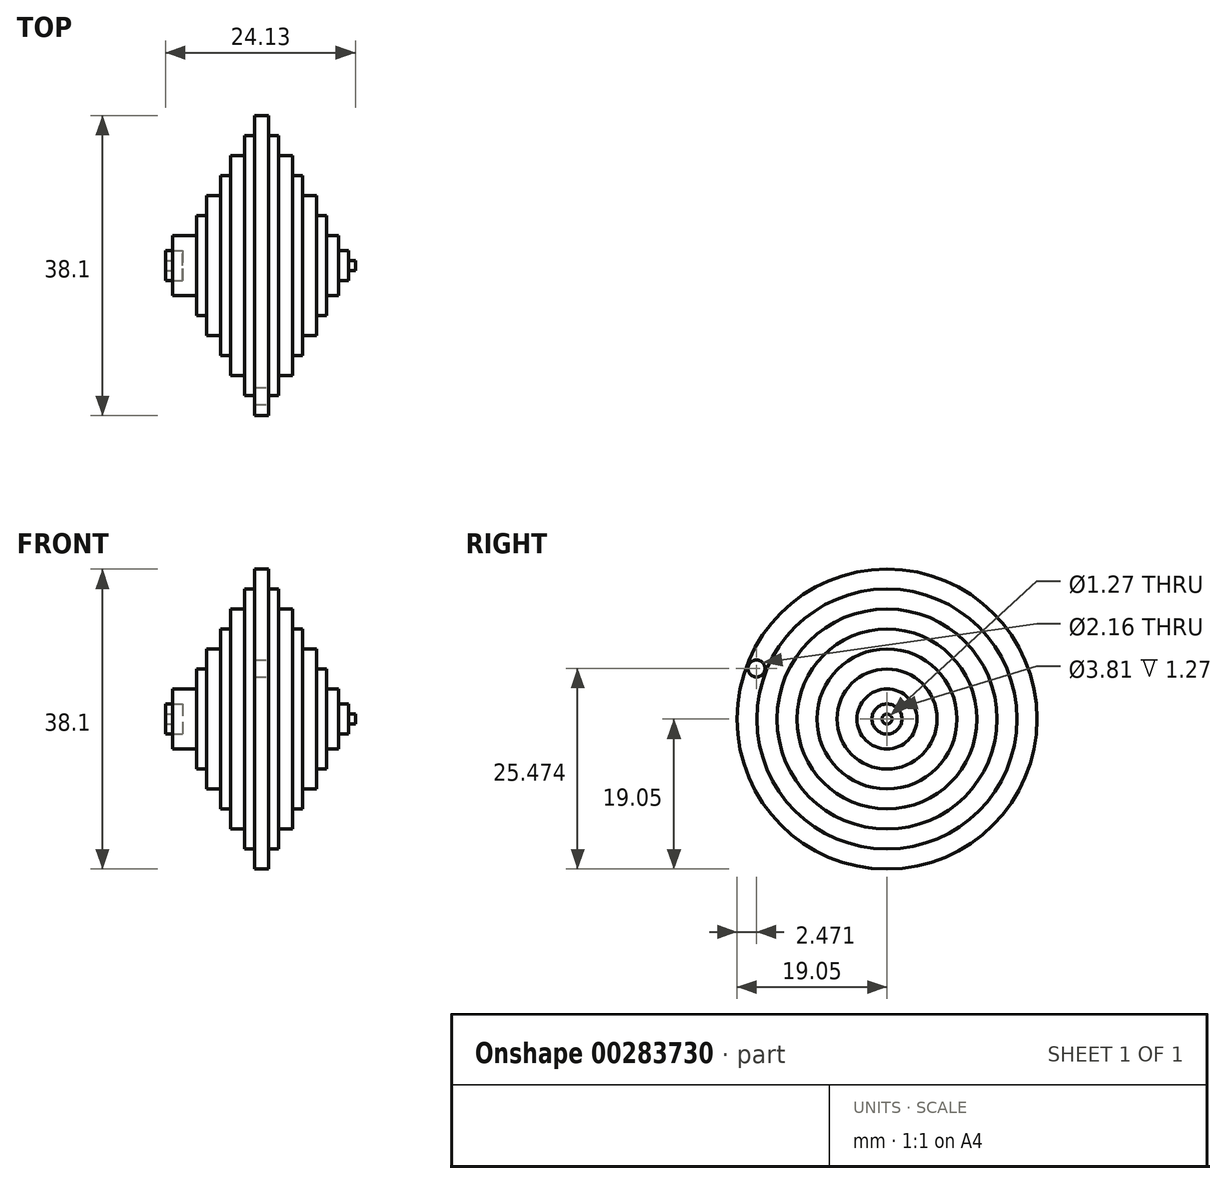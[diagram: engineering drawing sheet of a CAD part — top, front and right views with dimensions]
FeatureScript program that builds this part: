
annotation { "Feature Type Name" : "Feature", "Feature Type Description" : "" }
export const myFeature = defineFeature(function(context is Context, id is Id, definition is map)
    precondition{}
    {
        {
            var Q0;
            Q0=qCreatedBy(makeId("Right.planeOp"),FACE);
            var sketch = newSketch(context, id + "F0", { "sketchPlane" : qUnion([Q0])});
            skLineSegment(sketch, "E0", {"start": v(0, 0) * mm, "end": v(0, 38.1) * mm});
            skLineSegment(sketch, "E1", {"start": v(0, 38.1) * mm, "end": v(-38.1, 38.1) * mm});
            skLineSegment(sketch, "E2", {"start": v(-38.1, 38.1) * mm, "end": v(-38.1, 0) * mm});
            skLineSegment(sketch, "E3", {"start": v(-38.1, 0) * mm, "end": v(0, 0) * mm});
            skPoint(sketch, "E4.start.orphan", {"position": v(0.74, 0) * mm});
            skCircle(sketch, "E5", {"center": v(-19.05, 19.05) * mm, "radius": 19.05 * mm});
            skPoint(sketch, "E6.orphan", {"position": v(-19.05, 38.1) * mm});
            skPoint(sketch, "E7.end.orphan", {"position": v(-19.05, 0) * mm});
            skSolve(sketch);
        }
        {
            var Q0;
            {var subQ0=sQuery(id+"F0.wireOp",EDGE,"E5");var subQ1=makeQuery(id+"F0.imprint","INTERSECT",VERTEX,{"derivedFrom":[sQuery(id+"F0.wireOp",EDGE,"E0"),subQ0]});Q0=makeQuery(id+"F0.imprint","IMPRINT",FACE,{"disambiguationData":[TD([[makeQuery(id+"F0.imprint","IMPRINT",EDGE,{"disambiguationData":[TD([[subQ1,-1.0]])],"derivedFrom":subQ0}),1.0]])]});}
            extrude(context, id + "F1", {"entities" : qUnion([Q0]), "depth" : 1.78 * mm});
        }
        {
            var Q0;
            Q0=makeQuery(id+"F1.opExtrude","CAP_FACE",FACE,{"disambiguationData":[OSD([sQuery(id+"F0.wireOp",EDGE,"E5")])],"isStart":false});
            var sketch = newSketch(context, id + "F2", { "sketchPlane" : qUnion([Q0])});
            skLineSegment(sketch, "E8", {"start": v(0, 0) * mm, "end": v(0, 38.1) * mm});
            skLineSegment(sketch, "E9", {"start": v(0, 38.1) * mm, "end": v(-38.1, 38.1) * mm});
            skLineSegment(sketch, "E10", {"start": v(-38.1, 38.1) * mm, "end": v(-38.1, 0) * mm});
            skLineSegment(sketch, "E11", {"start": v(-38.1, 0) * mm, "end": v(0, 0) * mm});
            skCircle(sketch, "E12", {"center": v(-19.05, 19.05) * mm, "radius": 16.51 * mm});
            skPoint(sketch, "E13.start.orphan", {"position": v(-19.05, 38.1) * mm});
            skPoint(sketch, "E14.trimOffspring.end.orphan", {"position": v(-19.05, 0) * mm});
            skSolve(sketch);
        }
        {
            var Q0;
            Q0=makeQuery(id+"F2.imprint","IMPRINT",FACE,{"disambiguationData":[TD([[makeQuery(id+"F2.imprint","IMPRINT",EDGE,{"derivedFrom":sQuery(id+"F2.wireOp",EDGE,"E12")}),1.0]])]});
            extrude(context, id + "F3", {"entities" : qUnion([Q0]), "operationType" : NewBodyOperationType.ADD, "depth" : 1.27 * mm});
        }
        {
            var Q0;
            Q0=makeQuery(id+"F3.opExtrude","CAP_FACE",FACE,{"disambiguationData":[OSD([sQuery(id+"F2.wireOp",EDGE,"E12")])],"isStart":false});
            var sketch = newSketch(context, id + "F4", { "sketchPlane" : qUnion([Q0])});
            skLineSegment(sketch, "E15", {"start": v(0, 0) * mm, "end": v(-38.1, 0) * mm});
            skLineSegment(sketch, "E16", {"start": v(0, 38.1) * mm, "end": v(0, 0) * mm});
            skLineSegment(sketch, "E17", {"start": v(0, 38.1) * mm, "end": v(-38.1, 38.1) * mm});
            skLineSegment(sketch, "E18", {"start": v(-38.1, 38.1) * mm, "end": v(-38.1, 0) * mm});
            skCircle(sketch, "E19", {"center": v(-19.05, 19.05) * mm, "radius": 13.97 * mm});
            skPoint(sketch, "E20.start.orphan", {"position": v(-19.05, 38.1) * mm});
            skPoint(sketch, "E21.trimOffspring.end.orphan", {"position": v(-19.05, 0) * mm});
            skSolve(sketch);
        }
        {
            var Q0;
            Q0=makeQuery(id+"F4.imprint","IMPRINT",FACE,{"disambiguationData":[TD([[makeQuery(id+"F4.imprint","IMPRINT",EDGE,{"derivedFrom":sQuery(id+"F4.wireOp",EDGE,"E19")}),1.0]])]});
            extrude(context, id + "F5", {"entities" : qUnion([Q0]), "operationType" : NewBodyOperationType.ADD, "depth" : 1.78 * mm});
        }
        {
            var Q0;
            Q0=makeQuery(id+"F5.opExtrude","CAP_FACE",FACE,{"disambiguationData":[OSD([sQuery(id+"F4.wireOp",EDGE,"E19")])],"isStart":false});
            var sketch = newSketch(context, id + "F6", { "sketchPlane" : qUnion([Q0])});
            skLineSegment(sketch, "E22", {"start": v(0, 0) * mm, "end": v(0, 38.1) * mm});
            skLineSegment(sketch, "E23", {"start": v(0, 38.1) * mm, "end": v(-38.1, 38.1) * mm});
            skLineSegment(sketch, "E24", {"start": v(-38.1, 38.1) * mm, "end": v(-38.1, 0) * mm});
            skLineSegment(sketch, "E25", {"start": v(-38.1, 0) * mm, "end": v(0, 0) * mm});
            skCircle(sketch, "E26", {"center": v(-19.05, 19.05) * mm, "radius": 11.43 * mm});
            skPoint(sketch, "E27.start.orphan", {"position": v(-19.05, 38.1) * mm});
            skPoint(sketch, "E28.trimOffspring.end.orphan", {"position": v(-19.05, 0) * mm});
            skSolve(sketch);
        }
        {
            var Q0;
            Q0=makeQuery(id+"F6.imprint","IMPRINT",FACE,{"disambiguationData":[TD([[makeQuery(id+"F6.imprint","IMPRINT",EDGE,{"derivedFrom":sQuery(id+"F6.wireOp",EDGE,"E26")}),1.0]])]});
            extrude(context, id + "F7", {"entities" : qUnion([Q0]), "operationType" : NewBodyOperationType.ADD, "depth" : 1.27 * mm});
        }
        {
            var Q0;
            Q0=makeQuery(id+"F7.opExtrude","CAP_FACE",FACE,{"disambiguationData":[OSD([sQuery(id+"F6.wireOp",EDGE,"E26")])],"isStart":false});
            var sketch = newSketch(context, id + "F8", { "sketchPlane" : qUnion([Q0])});
            skLineSegment(sketch, "E29", {"start": v(0, 0) * mm, "end": v(0, 38.1) * mm});
            skLineSegment(sketch, "E30", {"start": v(0, 38.1) * mm, "end": v(-38.1, 38.1) * mm});
            skLineSegment(sketch, "E31", {"start": v(-38.1, 38.1) * mm, "end": v(-38.1, 0) * mm});
            skLineSegment(sketch, "E32", {"start": v(-38.1, 0) * mm, "end": v(0, 0) * mm});
            skCircle(sketch, "E33", {"center": v(-19.05, 19.05) * mm, "radius": 8.9 * mm});
            skPoint(sketch, "E34.start.orphan", {"position": v(-19.05, 38.1) * mm});
            skPoint(sketch, "E35.trimOffspring.end.orphan", {"position": v(-19.05, 0) * mm});
            skSolve(sketch);
        }
        {
            var Q0;
            Q0=makeQuery(id+"F8.imprint","IMPRINT",FACE,{"disambiguationData":[TD([[makeQuery(id+"F8.imprint","IMPRINT",EDGE,{"derivedFrom":sQuery(id+"F8.wireOp",EDGE,"E33")}),1.0]])]});
            extrude(context, id + "F9", {"entities" : qUnion([Q0]), "operationType" : NewBodyOperationType.ADD, "depth" : 1.78 * mm});
        }
        {
            var Q0;
            Q0=makeQuery(id+"F9.opExtrude","CAP_FACE",FACE,{"disambiguationData":[OSD([sQuery(id+"F8.wireOp",EDGE,"E33")])],"isStart":false});
            var sketch = newSketch(context, id + "F10", { "sketchPlane" : qUnion([Q0])});
            skLineSegment(sketch, "E36", {"start": v(0, 0) * mm, "end": v(0, 38.1) * mm});
            skLineSegment(sketch, "E37", {"start": v(0, 38.1) * mm, "end": v(-38.1, 38.1) * mm});
            skLineSegment(sketch, "E38", {"start": v(-38.1, 38.1) * mm, "end": v(-38.1, 0) * mm});
            skLineSegment(sketch, "E39", {"start": v(-38.1, 0) * mm, "end": v(0, -0.59) * mm});
            skCircle(sketch, "E40", {"center": v(-19.05, 19.05) * mm, "radius": 6.35 * mm});
            skPoint(sketch, "E41.orphan", {"position": v(-19.05, 38.1) * mm});
            skPoint(sketch, "E42.end.orphan", {"position": v(-19.05, -0.3) * mm});
            skSolve(sketch);
        }
        {
            var Q0;
            Q0=makeQuery(id+"F10.imprint","IMPRINT",FACE,{"disambiguationData":[TD([[makeQuery(id+"F10.imprint","IMPRINT",EDGE,{"derivedFrom":sQuery(id+"F10.wireOp",EDGE,"E40")}),1.0]])]});
            extrude(context, id + "F11", {"entities" : qUnion([Q0]), "operationType" : NewBodyOperationType.ADD, "depth" : 1.27 * mm});
        }
        {
            var Q0;
            Q0=makeQuery(id+"F11.opExtrude","CAP_FACE",FACE,{"disambiguationData":[OSD([sQuery(id+"F10.wireOp",EDGE,"E40")])],"isStart":false});
            var sketch = newSketch(context, id + "F12", { "sketchPlane" : qUnion([Q0])});
            skLineSegment(sketch, "E43", {"start": v(0, 0) * mm, "end": v(0, 38.1) * mm});
            skLineSegment(sketch, "E44", {"start": v(0, 38.1) * mm, "end": v(-38.1, 38.1) * mm});
            skLineSegment(sketch, "E45", {"start": v(-38.1, 38.1) * mm, "end": v(-38.1, 0) * mm});
            skLineSegment(sketch, "E46", {"start": v(-38.1, 0) * mm, "end": v(0, 0) * mm});
            skCircle(sketch, "E47", {"center": v(-19.05, 19.05) * mm, "radius": 3.81 * mm});
            skPoint(sketch, "E48.orphan", {"position": v(-19.05, 38.1) * mm});
            skPoint(sketch, "E49.end.orphan", {"position": v(-19.05, 0) * mm});
            skSolve(sketch);
        }
        {
            var Q0;
            Q0=makeQuery(id+"F12.imprint","IMPRINT",FACE,{"disambiguationData":[TD([[makeQuery(id+"F12.imprint","IMPRINT",EDGE,{"derivedFrom":sQuery(id+"F12.wireOp",EDGE,"E47")}),1.0]])]});
            extrude(context, id + "F13", {"entities" : qUnion([Q0]), "operationType" : NewBodyOperationType.ADD, "depth" : 1.52 * mm});
        }
        {
            var Q0;
            Q0=makeQuery(id+"F13.opExtrude","CAP_FACE",FACE,{"disambiguationData":[OSD([sQuery(id+"F12.wireOp",EDGE,"E47")])],"isStart":false});
            var sketch = newSketch(context, id + "F14", { "sketchPlane" : qUnion([Q0])});
            skLineSegment(sketch, "E50", {"start": v(0, 0) * mm, "end": v(0, 38.1) * mm});
            skLineSegment(sketch, "E51", {"start": v(0, 38.1) * mm, "end": v(-38.1, 38.1) * mm});
            skLineSegment(sketch, "E52", {"start": v(-38.1, 38.1) * mm, "end": v(-38.1, 0) * mm});
            skLineSegment(sketch, "E53", {"start": v(-38.1, 0) * mm, "end": v(0, 0) * mm});
            skCircle(sketch, "E54", {"center": v(-19.05, 19.05) * mm, "radius": 1.9 * mm});
            skPoint(sketch, "E55.orphan", {"position": v(-19.05, 38.1) * mm});
            skPoint(sketch, "E56.end.orphan", {"position": v(-19.05, 0) * mm});
            skSolve(sketch);
        }
        {
            var Q0;
            Q0=makeQuery(id+"F14.imprint","IMPRINT",FACE,{"disambiguationData":[TD([[makeQuery(id+"F14.imprint","IMPRINT",EDGE,{"derivedFrom":sQuery(id+"F14.wireOp",EDGE,"E54")}),1.0]])]});
            extrude(context, id + "F15", {"entities" : qUnion([Q0]), "operationType" : NewBodyOperationType.ADD, "depth" : 1.27 * mm});
        }
        {
            var Q0;
            Q0=makeQuery(id+"F15.opExtrude","CAP_FACE",FACE,{"disambiguationData":[OSD([sQuery(id+"F14.wireOp",EDGE,"E54")])],"isStart":false});
            var sketch = newSketch(context, id + "F16", { "sketchPlane" : qUnion([Q0])});
            skLineSegment(sketch, "E57", {"start": v(0, 0) * mm, "end": v(0, 38.1) * mm});
            skLineSegment(sketch, "E58", {"start": v(0, 38.1) * mm, "end": v(-38.1, 38.1) * mm});
            skLineSegment(sketch, "E59", {"start": v(-38.1, 38.1) * mm, "end": v(-38.1, 0) * mm});
            skLineSegment(sketch, "E60", {"start": v(-38.1, 0) * mm, "end": v(0, 0) * mm});
            skCircle(sketch, "E61", {"center": v(-19.05, 19.05) * mm, "radius": 0.64 * mm});
            skPoint(sketch, "E62.orphan", {"position": v(-19.05, 38.1) * mm});
            skPoint(sketch, "E63.end.orphan", {"position": v(-19.05, 0) * mm});
            skSolve(sketch);
        }
        {
            var Q0;
            Q0=makeQuery(id+"F16.imprint","IMPRINT",FACE,{"disambiguationData":[TD([[makeQuery(id+"F16.imprint","IMPRINT",EDGE,{"derivedFrom":sQuery(id+"F16.wireOp",EDGE,"E61")}),1.0]])]});
            extrude(context, id + "F17", {"entities" : qUnion([Q0]), "operationType" : NewBodyOperationType.ADD, "depth" : 0.89 * mm});
        }
        {
            var Q0;
            Q0=makeQuery(id+"F1.opExtrude","CAP_FACE",FACE,{"disambiguationData":[OSD([sQuery(id+"F0.wireOp",EDGE,"E5")])],"isStart":false});
            var sketch = newSketch(context, id + "F18", { "sketchPlane" : qUnion([Q0])});
            skCircle(sketch, "E64", {"center": v(-35.63, 25.47) * mm, "radius": 1.08 * mm});
            skPoint(sketch, "E65.trimOffspring.end.orphan", {"position": v(-34.49, 24.9) * mm});
            skPoint(sketch, "E66.start.orphan", {"position": v(-36.77, 26.05) * mm});
            skSolve(sketch);
        }
        {
            var Q0;
            Q0=makeQuery(id+"F18.imprint","IMPRINT",FACE,{"disambiguationData":[TD([[makeQuery(id+"F18.imprint","IMPRINT",EDGE,{"derivedFrom":sQuery(id+"F18.wireOp",EDGE,"E64")}),1.0]])]});
            extrude(context, id + "F19", {"entities" : qUnion([Q0]), "operationType" : NewBodyOperationType.REMOVE, "oppositeDirection" : true, "depth" : 1.78 * mm});
        }
        {
            var Q0;
            Q0=makeQuery(id+"F1.opExtrude","CAP_FACE",FACE,{"disambiguationData":[OSD([sQuery(id+"F0.wireOp",EDGE,"E5")])],"isStart":true});
            var sketch = newSketch(context, id + "F20", { "sketchPlane" : qUnion([Q0])});
            skLineSegment(sketch, "E67", {"start": v(0, 0) * mm, "end": v(0, 38.1) * mm});
            skLineSegment(sketch, "E68", {"start": v(0, 38.1) * mm, "end": v(38.1, 38.1) * mm});
            skLineSegment(sketch, "E69", {"start": v(38.1, 38.1) * mm, "end": v(38.1, 0) * mm});
            skLineSegment(sketch, "E70", {"start": v(38.1, 0) * mm, "end": v(0, 0) * mm});
            skLineSegment(sketch, "E71", {"start": v(19.05, 38.1) * mm, "end": v(19.05, 0) * mm});
            skCircle(sketch, "E72", {"center": v(19.05, 19.05) * mm, "radius": 16.51 * mm});
            skSolve(sketch);
        }
        {
            var Q0;
            {var subQ0=sQuery(id+"F20.wireOp",EDGE,"E72");var subQ1=sQuery(id+"F20.wireOp",EDGE,"E71");var subQ2=makeQuery(id+"F20.imprint","INTERSECT",VERTEX,{"disambiguationData":[OD(0.0)],"derivedFrom":[subQ1,subQ0]});Q0=makeQuery(id+"F20.imprint","IMPRINT",FACE,{"disambiguationData":[TD([[makeQuery(id+"F20.imprint","IMPRINT",EDGE,{"disambiguationData":[TD([[subQ2,-1.0]])],"derivedFrom":subQ1}),-1.0]])]});}
            var Q1;
            {var subQ0=sQuery(id+"F20.wireOp",EDGE,"E72");var subQ1=sQuery(id+"F20.wireOp",EDGE,"E71");var subQ2=makeQuery(id+"F20.imprint","INTERSECT",VERTEX,{"disambiguationData":[OD(0.0)],"derivedFrom":[subQ1,subQ0]});Q1=makeQuery(id+"F20.imprint","IMPRINT",FACE,{"disambiguationData":[TD([[makeQuery(id+"F20.imprint","IMPRINT",EDGE,{"disambiguationData":[TD([[subQ2,-1.0]])],"derivedFrom":subQ1}),1.0]])]});}
            extrude(context, id + "F21", {"entities" : qUnion([Q0, Q1]), "operationType" : NewBodyOperationType.ADD, "depth" : 1.27 * mm});
        }
        {
            var Q0;
            Q0=makeQuery(id+"F21.opExtrude","CAP_FACE",FACE,{"disambiguationData":[OSD([sQuery(id+"F20.wireOp",EDGE,"E72")])],"isStart":false});
            var sketch = newSketch(context, id + "F22", { "sketchPlane" : qUnion([Q0])});
            skLineSegment(sketch, "E73", {"start": v(0, 0) * mm, "end": v(0, 38.1) * mm});
            skLineSegment(sketch, "E74", {"start": v(0, 38.1) * mm, "end": v(38.1, 38.1) * mm});
            skLineSegment(sketch, "E75", {"start": v(38.1, 38.1) * mm, "end": v(38.1, 0) * mm});
            skLineSegment(sketch, "E76", {"start": v(38.1, 0) * mm, "end": v(0, 0) * mm});
            skLineSegment(sketch, "E77", {"start": v(19.05, 38.1) * mm, "end": v(19.05, 0) * mm});
            skCircle(sketch, "E78", {"center": v(19.05, 19.05) * mm, "radius": 13.97 * mm});
            skSolve(sketch);
        }
        {
            var Q0;
            {var subQ0=sQuery(id+"F22.wireOp",EDGE,"E78");var subQ1=sQuery(id+"F22.wireOp",EDGE,"E77");var subQ2=makeQuery(id+"F22.imprint","INTERSECT",VERTEX,{"disambiguationData":[OD(0.0)],"derivedFrom":[subQ1,subQ0]});Q0=makeQuery(id+"F22.imprint","IMPRINT",FACE,{"disambiguationData":[TD([[makeQuery(id+"F22.imprint","IMPRINT",EDGE,{"disambiguationData":[TD([[subQ2,-1.0]])],"derivedFrom":subQ1}),-1.0]])]});}
            var Q1;
            {var subQ0=sQuery(id+"F22.wireOp",EDGE,"E78");var subQ1=sQuery(id+"F22.wireOp",EDGE,"E77");var subQ2=makeQuery(id+"F22.imprint","INTERSECT",VERTEX,{"disambiguationData":[OD(0.0)],"derivedFrom":[subQ1,subQ0]});Q1=makeQuery(id+"F22.imprint","IMPRINT",FACE,{"disambiguationData":[TD([[makeQuery(id+"F22.imprint","IMPRINT",EDGE,{"disambiguationData":[TD([[subQ2,-1.0]])],"derivedFrom":subQ1}),1.0]])]});}
            extrude(context, id + "F23", {"entities" : qUnion([Q0, Q1]), "operationType" : NewBodyOperationType.ADD, "depth" : 1.78 * mm});
        }
        {
            var Q0;
            Q0=makeQuery(id+"F23.opExtrude","CAP_FACE",FACE,{"disambiguationData":[OSD([sQuery(id+"F22.wireOp",EDGE,"E78")])],"isStart":false});
            var sketch = newSketch(context, id + "F24", { "sketchPlane" : qUnion([Q0])});
            skLineSegment(sketch, "E79", {"start": v(0, 0) * mm, "end": v(38.1, 0) * mm});
            skLineSegment(sketch, "E80", {"start": v(38.1, 0) * mm, "end": v(38.1, 38.1) * mm});
            skLineSegment(sketch, "E81", {"start": v(38.1, 38.1) * mm, "end": v(0, 38.1) * mm});
            skLineSegment(sketch, "E82", {"start": v(0, 38.1) * mm, "end": v(0, 0) * mm});
            skLineSegment(sketch, "E83", {"start": v(19.05, 38.1) * mm, "end": v(19.05, 0) * mm});
            skCircle(sketch, "E84", {"center": v(19.05, 19.05) * mm, "radius": 11.43 * mm});
            skSolve(sketch);
        }
        {
            var Q0;
            {var subQ0=sQuery(id+"F24.wireOp",EDGE,"E84");var subQ1=sQuery(id+"F24.wireOp",EDGE,"E83");var subQ2=makeQuery(id+"F24.imprint","INTERSECT",VERTEX,{"disambiguationData":[OD(0.0)],"derivedFrom":[subQ1,subQ0]});Q0=makeQuery(id+"F24.imprint","IMPRINT",FACE,{"disambiguationData":[TD([[makeQuery(id+"F24.imprint","IMPRINT",EDGE,{"disambiguationData":[TD([[subQ2,-1.0]])],"derivedFrom":subQ1}),1.0]])]});}
            var Q1;
            {var subQ0=sQuery(id+"F24.wireOp",EDGE,"E84");var subQ1=sQuery(id+"F24.wireOp",EDGE,"E83");var subQ2=makeQuery(id+"F24.imprint","INTERSECT",VERTEX,{"disambiguationData":[OD(0.0)],"derivedFrom":[subQ1,subQ0]});Q1=makeQuery(id+"F24.imprint","IMPRINT",FACE,{"disambiguationData":[TD([[makeQuery(id+"F24.imprint","IMPRINT",EDGE,{"disambiguationData":[TD([[subQ2,-1.0]])],"derivedFrom":subQ1}),-1.0]])]});}
            extrude(context, id + "F25", {"entities" : qUnion([Q0, Q1]), "operationType" : NewBodyOperationType.ADD, "depth" : 1.27 * mm});
        }
        {
            var Q0;
            Q0=makeQuery(id+"F25.opExtrude","CAP_FACE",FACE,{"disambiguationData":[OSD([sQuery(id+"F24.wireOp",EDGE,"E84")])],"isStart":false});
            var sketch = newSketch(context, id + "F26", { "sketchPlane" : qUnion([Q0])});
            skLineSegment(sketch, "E85", {"start": v(0, 0) * mm, "end": v(0, 38.1) * mm});
            skLineSegment(sketch, "E86", {"start": v(0, 38.1) * mm, "end": v(38.1, 38.1) * mm});
            skLineSegment(sketch, "E87", {"start": v(38.1, 38.1) * mm, "end": v(38.1, 0) * mm});
            skLineSegment(sketch, "E88", {"start": v(38.1, 0) * mm, "end": v(0, 0) * mm});
            skLineSegment(sketch, "E89", {"start": v(19.05, 38.1) * mm, "end": v(19.05, 0) * mm});
            skCircle(sketch, "E90", {"center": v(19.05, 19.05) * mm, "radius": 8.9 * mm});
            skSolve(sketch);
        }
        {
            var Q0;
            {var subQ0=sQuery(id+"F26.wireOp",EDGE,"E90");var subQ1=sQuery(id+"F26.wireOp",EDGE,"E89");var subQ2=makeQuery(id+"F26.imprint","INTERSECT",VERTEX,{"disambiguationData":[OD(0.0)],"derivedFrom":[subQ1,subQ0]});Q0=makeQuery(id+"F26.imprint","IMPRINT",FACE,{"disambiguationData":[TD([[makeQuery(id+"F26.imprint","IMPRINT",EDGE,{"disambiguationData":[TD([[subQ2,-1.0]])],"derivedFrom":subQ1}),-1.0]])]});}
            var Q1;
            {var subQ0=sQuery(id+"F26.wireOp",EDGE,"E90");var subQ1=sQuery(id+"F26.wireOp",EDGE,"E89");var subQ2=makeQuery(id+"F26.imprint","INTERSECT",VERTEX,{"disambiguationData":[OD(0.0)],"derivedFrom":[subQ1,subQ0]});Q1=makeQuery(id+"F26.imprint","IMPRINT",FACE,{"disambiguationData":[TD([[makeQuery(id+"F26.imprint","IMPRINT",EDGE,{"disambiguationData":[TD([[subQ2,-1.0]])],"derivedFrom":subQ1}),1.0]])]});}
            extrude(context, id + "F27", {"entities" : qUnion([Q0, Q1]), "operationType" : NewBodyOperationType.ADD, "depth" : 1.78 * mm});
        }
        {
            var Q0;
            Q0=makeQuery(id+"F27.opExtrude","CAP_FACE",FACE,{"disambiguationData":[OSD([sQuery(id+"F26.wireOp",EDGE,"E90")])],"isStart":false});
            var sketch = newSketch(context, id + "F28", { "sketchPlane" : qUnion([Q0])});
            skLineSegment(sketch, "E91", {"start": v(0, 0) * mm, "end": v(0, 38.1) * mm});
            skLineSegment(sketch, "E92", {"start": v(0, 38.1) * mm, "end": v(38.1, 38.1) * mm});
            skLineSegment(sketch, "E93", {"start": v(38.1, 38.1) * mm, "end": v(38.1, 0) * mm});
            skLineSegment(sketch, "E94", {"start": v(38.1, 0) * mm, "end": v(0, 0) * mm});
            skLineSegment(sketch, "E95", {"start": v(19.05, 38.1) * mm, "end": v(19.05, 0) * mm});
            skCircle(sketch, "E96", {"center": v(19.05, 19.05) * mm, "radius": 6.35 * mm});
            skSolve(sketch);
        }
        {
            var Q0;
            {var subQ0=sQuery(id+"F28.wireOp",EDGE,"E96");var subQ1=sQuery(id+"F28.wireOp",EDGE,"E95");var subQ2=makeQuery(id+"F28.imprint","INTERSECT",VERTEX,{"disambiguationData":[OD(0.0)],"derivedFrom":[subQ1,subQ0]});Q0=makeQuery(id+"F28.imprint","IMPRINT",FACE,{"disambiguationData":[TD([[makeQuery(id+"F28.imprint","IMPRINT",EDGE,{"disambiguationData":[TD([[subQ2,-1.0]])],"derivedFrom":subQ1}),-1.0]])]});}
            var Q1;
            {var subQ0=sQuery(id+"F28.wireOp",EDGE,"E96");var subQ1=sQuery(id+"F28.wireOp",EDGE,"E95");var subQ2=makeQuery(id+"F28.imprint","INTERSECT",VERTEX,{"disambiguationData":[OD(0.0)],"derivedFrom":[subQ1,subQ0]});Q1=makeQuery(id+"F28.imprint","IMPRINT",FACE,{"disambiguationData":[TD([[makeQuery(id+"F28.imprint","IMPRINT",EDGE,{"disambiguationData":[TD([[subQ2,-1.0]])],"derivedFrom":subQ1}),1.0]])]});}
            extrude(context, id + "F29", {"entities" : qUnion([Q0, Q1]), "operationType" : NewBodyOperationType.ADD, "depth" : 1.27 * mm});
        }
        {
            var Q0;
            Q0=makeQuery(id+"F29.opExtrude","CAP_FACE",FACE,{"disambiguationData":[OSD([sQuery(id+"F28.wireOp",EDGE,"E96")])],"isStart":false});
            var sketch = newSketch(context, id + "F30", { "sketchPlane" : qUnion([Q0])});
            skLineSegment(sketch, "E97", {"start": v(0, 0) * mm, "end": v(0, 38.1) * mm});
            skLineSegment(sketch, "E98", {"start": v(0, 38.1) * mm, "end": v(38.1, 38.1) * mm});
            skLineSegment(sketch, "E99", {"start": v(38.1, 38.1) * mm, "end": v(38.1, 0) * mm});
            skLineSegment(sketch, "E100", {"start": v(38.1, 0) * mm, "end": v(0, 0) * mm});
            skLineSegment(sketch, "E101", {"start": v(19.05, 38.1) * mm, "end": v(19.05, 0) * mm});
            skCircle(sketch, "E102", {"center": v(19.05, 19.05) * mm, "radius": 3.81 * mm});
            skSolve(sketch);
        }
        {
            var Q0;
            {var subQ0=sQuery(id+"F30.wireOp",EDGE,"E102");var subQ1=sQuery(id+"F30.wireOp",EDGE,"E101");var subQ2=makeQuery(id+"F30.imprint","INTERSECT",VERTEX,{"disambiguationData":[OD(0.0)],"derivedFrom":[subQ1,subQ0]});Q0=makeQuery(id+"F30.imprint","IMPRINT",FACE,{"disambiguationData":[TD([[makeQuery(id+"F30.imprint","IMPRINT",EDGE,{"disambiguationData":[TD([[subQ2,-1.0]])],"derivedFrom":subQ1}),-1.0]])]});}
            var Q1;
            {var subQ0=sQuery(id+"F30.wireOp",EDGE,"E102");var subQ1=sQuery(id+"F30.wireOp",EDGE,"E101");var subQ2=makeQuery(id+"F30.imprint","INTERSECT",VERTEX,{"disambiguationData":[OD(0.0)],"derivedFrom":[subQ1,subQ0]});Q1=makeQuery(id+"F30.imprint","IMPRINT",FACE,{"disambiguationData":[TD([[makeQuery(id+"F30.imprint","IMPRINT",EDGE,{"disambiguationData":[TD([[subQ2,-1.0]])],"derivedFrom":subQ1}),1.0]])]});}
            extrude(context, id + "F31", {"entities" : qUnion([Q0, Q1]), "operationType" : NewBodyOperationType.ADD, "depth" : 1.78 * mm});
        }
        {
            var Q0;
            Q0=makeQuery(id+"F31.opExtrude","CAP_FACE",FACE,{"disambiguationData":[OSD([sQuery(id+"F30.wireOp",EDGE,"E102")])],"isStart":false});
            var sketch = newSketch(context, id + "F32", { "sketchPlane" : qUnion([Q0])});
            skLineSegment(sketch, "E103", {"start": v(0, 0) * mm, "end": v(0, 38.1) * mm});
            skLineSegment(sketch, "E104", {"start": v(0, 38.1) * mm, "end": v(38.1, 38.1) * mm});
            skLineSegment(sketch, "E105", {"start": v(38.1, 38.1) * mm, "end": v(38.1, 0) * mm});
            skLineSegment(sketch, "E106", {"start": v(38.1, 0) * mm, "end": v(0, 0) * mm});
            skLineSegment(sketch, "E107", {"start": v(19.05, 38.1) * mm, "end": v(19.05, 0) * mm});
            skCircle(sketch, "E108", {"center": v(19.05, 19.05) * mm, "radius": 1.9 * mm});
            skSolve(sketch);
        }
        {
            var Q0;
            {var subQ0=sQuery(id+"F32.wireOp",EDGE,"E108");var subQ1=sQuery(id+"F32.wireOp",EDGE,"E107");var subQ2=makeQuery(id+"F32.imprint","INTERSECT",VERTEX,{"disambiguationData":[OD(0.0)],"derivedFrom":[subQ1,subQ0]});Q0=makeQuery(id+"F32.imprint","IMPRINT",FACE,{"disambiguationData":[TD([[makeQuery(id+"F32.imprint","IMPRINT",EDGE,{"disambiguationData":[TD([[subQ2,-1.0]])],"derivedFrom":subQ1}),1.0]])]});}
            var Q1;
            {var subQ0=sQuery(id+"F32.wireOp",EDGE,"E108");var subQ1=sQuery(id+"F32.wireOp",EDGE,"E107");var subQ2=makeQuery(id+"F32.imprint","INTERSECT",VERTEX,{"disambiguationData":[OD(0.0)],"derivedFrom":[subQ1,subQ0]});Q1=makeQuery(id+"F32.imprint","IMPRINT",FACE,{"disambiguationData":[TD([[makeQuery(id+"F32.imprint","IMPRINT",EDGE,{"disambiguationData":[TD([[subQ2,-1.0]])],"derivedFrom":subQ1}),-1.0]])]});}
            extrude(context, id + "F33", {"entities" : qUnion([Q0, Q1]), "operationType" : NewBodyOperationType.ADD, "depth" : 1.27 * mm});
        }
        {
            var Q0;
            Q0=makeQuery(id+"F33.opExtrude","CAP_FACE",FACE,{"disambiguationData":[OSD([sQuery(id+"F32.wireOp",EDGE,"E108")])],"isStart":false});
            var sketch = newSketch(context, id + "F34", { "sketchPlane" : qUnion([Q0])});
            skLineSegment(sketch, "E109", {"start": v(0, 0) * mm, "end": v(0, 38.1) * mm});
            skLineSegment(sketch, "E110", {"start": v(0, 38.1) * mm, "end": v(38.1, 38.1) * mm});
            skLineSegment(sketch, "E111", {"start": v(38.1, 38.1) * mm, "end": v(38.1, 0) * mm});
            skLineSegment(sketch, "E112", {"start": v(38.1, 0) * mm, "end": v(0, 0) * mm});
            skLineSegment(sketch, "E113", {"start": v(19.05, 38.1) * mm, "end": v(19.05, 0) * mm});
            skCircle(sketch, "E114", {"center": v(19.05, 19.05) * mm, "radius": 0.64 * mm});
            skSolve(sketch);
        }
        {
            var Q0;
            {var subQ0=sQuery(id+"F34.wireOp",EDGE,"E114");var subQ1=sQuery(id+"F34.wireOp",EDGE,"E113");var subQ2=makeQuery(id+"F34.imprint","INTERSECT",VERTEX,{"disambiguationData":[OD(0.0)],"derivedFrom":[subQ1,subQ0]});Q0=makeQuery(id+"F34.imprint","IMPRINT",FACE,{"disambiguationData":[TD([[makeQuery(id+"F34.imprint","IMPRINT",EDGE,{"disambiguationData":[TD([[subQ2,-1.0]])],"derivedFrom":subQ1}),1.0]])]});}
            var Q1;
            {var subQ0=sQuery(id+"F34.wireOp",EDGE,"E114");var subQ1=sQuery(id+"F34.wireOp",EDGE,"E113");var subQ2=makeQuery(id+"F34.imprint","INTERSECT",VERTEX,{"disambiguationData":[OD(0.0)],"derivedFrom":[subQ1,subQ0]});Q1=makeQuery(id+"F34.imprint","IMPRINT",FACE,{"disambiguationData":[TD([[makeQuery(id+"F34.imprint","IMPRINT",EDGE,{"disambiguationData":[TD([[subQ2,-1.0]])],"derivedFrom":subQ1}),-1.0]])]});}
            extrude(context, id + "F35", {"entities" : qUnion([Q0, Q1]), "operationType" : NewBodyOperationType.ADD, "depth" : 0.89 * mm});
        }
    });
